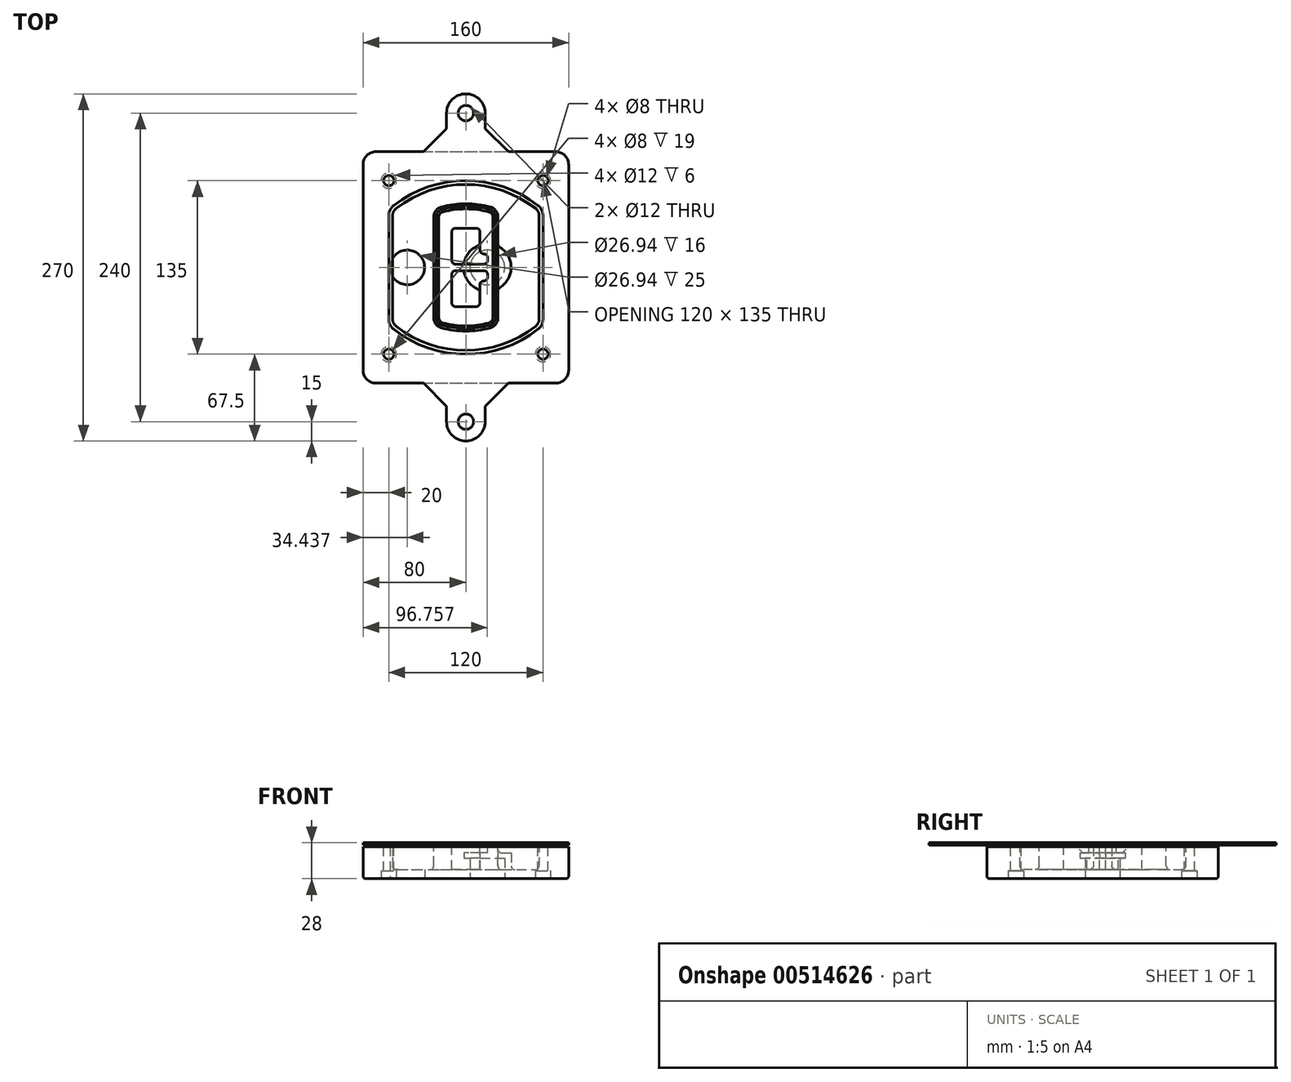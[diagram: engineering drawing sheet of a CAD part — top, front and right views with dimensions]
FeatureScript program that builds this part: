
annotation { "Feature Type Name" : "Feature", "Feature Type Description" : "" }
export const myFeature = defineFeature(function(context is Context, id is Id, definition is map)
    precondition{}
    {
        {
            var Q0;
            Q0=qCreatedBy(makeId("Top.planeOp"),FACE);
            var sketch = newSketch(context, id + "F0", { "sketchPlane" : qUnion([Q0])});
            skPoint(sketch, "E0.rect.middle", {"position": v(0, 0) * mm});
            skLineSegment(sketch, "E1.bottom", {"start": v(-70, -90) * mm, "end": v(70, -90) * mm});
            skLineSegment(sketch, "E1.top", {"start": v(-70, 90) * mm, "end": v(70, 90) * mm});
            skLineSegment(sketch, "E1.left", {"start": v(-80, -80) * mm, "end": v(-80, 80) * mm});
            skLineSegment(sketch, "E1.right", {"start": v(80, -80) * mm, "end": v(80, 80) * mm});
            skLineSegment(sketch, "E2", {"start": v(-80, 90) * mm, "end": v(80, -90) * mm, "construction": true});
            skLineSegment(sketch, "E3", {"start": v(80, 90) * mm, "end": v(-80, -90) * mm, "construction": true});
            skCircle(sketch, "E4", {"center": v(-60, 67.5) * mm, "radius": 4 * mm});
            skCircle(sketch, "E5", {"center": v(60, 67.5) * mm, "radius": 4 * mm});
            skCircle(sketch, "E6", {"center": v(60, -67.5) * mm, "radius": 4 * mm});
            skCircle(sketch, "E7", {"center": v(-60, -67.5) * mm, "radius": 4 * mm});
            skLineSegment(sketch, "E8", {"start": v(-60, 67.5) * mm, "end": v(60, 67.5) * mm, "construction": true});
            skLineSegment(sketch, "E9", {"start": v(60, 67.5) * mm, "end": v(60, -67.5) * mm, "construction": true});
            skLineSegment(sketch, "E10", {"start": v(60, -67.5) * mm, "end": v(-60, -67.5) * mm, "construction": true});
            skLineSegment(sketch, "E11", {"start": v(-60, -67.5) * mm, "end": v(-60, 67.5) * mm, "construction": true});
            skLineSegment(sketch, "E12", {"start": v(-60, 40.3) * mm, "end": v(-60, -40.3) * mm});
            skLineSegment(sketch, "E13", {"start": v(60, 40.3) * mm, "end": v(60, -40.3) * mm});
            skArc(sketch, "E14", {"start": v(56.15, 48.18) * mm, "mid": v(0, 67.5) * mm, "end": v(-56.15, 48.18) * mm});
            skArc(sketch, "E15", {"start": v(-56.15, -48.18) * mm, "mid": v(0, -67.5) * mm, "end": v(56.15, -48.18) * mm});
            skLineSegment(sketch, "E16", {"start": v(-60, 0) * mm, "end": v(60, 0) * mm, "construction": true});
            skPoint(sketch, "E17.visualSharp", {"position": v(-60, -45) * mm});
            skArc(sketch, "E17.filletArc", {"start": v(-60, -40.3) * mm, "mid": v(-58.99, -44.68) * mm, "end": v(-56.15, -48.18) * mm});
            skPoint(sketch, "E18.visualSharp", {"position": v(-60, 45) * mm});
            skArc(sketch, "E18.filletArc", {"start": v(-56.15, 48.18) * mm, "mid": v(-58.99, 44.68) * mm, "end": v(-60, 40.3) * mm});
            skPoint(sketch, "E19.visualSharp", {"position": v(60, 45) * mm});
            skArc(sketch, "E19.filletArc", {"start": v(60, 40.3) * mm, "mid": v(58.99, 44.68) * mm, "end": v(56.15, 48.18) * mm});
            skPoint(sketch, "E20.visualSharp", {"position": v(60, -45) * mm});
            skArc(sketch, "E20.filletArc", {"start": v(56.15, -48.18) * mm, "mid": v(58.99, -44.68) * mm, "end": v(60, -40.3) * mm});
            skPoint(sketch, "E21.visualSharp", {"position": v(-80, 90) * mm});
            skArc(sketch, "E21.filletArc", {"start": v(-70, 90) * mm, "mid": v(-77.07, 87.07) * mm, "end": v(-80, 80) * mm});
            skPoint(sketch, "E22.visualSharp", {"position": v(80, 90) * mm});
            skArc(sketch, "E22.filletArc", {"start": v(80, 80) * mm, "mid": v(77.07, 87.07) * mm, "end": v(70, 90) * mm});
            skPoint(sketch, "E23.visualSharp", {"position": v(80, -90) * mm});
            skArc(sketch, "E23.filletArc", {"start": v(70, -90) * mm, "mid": v(77.07, -87.07) * mm, "end": v(80, -80) * mm});
            skPoint(sketch, "E24.visualSharp", {"position": v(-80, -90) * mm});
            skArc(sketch, "E24.filletArc", {"start": v(-80, -80) * mm, "mid": v(-77.07, -87.07) * mm, "end": v(-70, -90) * mm});
            skArc(sketch, "E25.0", {"start": v(57, 40.3) * mm, "mid": v(56.3, 43.36) * mm, "end": v(54.3, 45.81) * mm});
            skLineSegment(sketch, "E25.1", {"start": v(57, 40.3) * mm, "end": v(57, -40.3) * mm});
            skArc(sketch, "E25.2", {"start": v(54.3, -45.81) * mm, "mid": v(56.3, -43.36) * mm, "end": v(57, -40.3) * mm});
            skArc(sketch, "E25.3", {"start": v(-54.3, -45.81) * mm, "mid": v(0, -64.5) * mm, "end": v(54.3, -45.81) * mm});
            skArc(sketch, "E25.4", {"start": v(-57, -40.3) * mm, "mid": v(-56.3, -43.36) * mm, "end": v(-54.3, -45.81) * mm});
            skArc(sketch, "E25.5", {"start": v(54.3, 45.81) * mm, "mid": v(0, 64.5) * mm, "end": v(-54.3, 45.81) * mm});
            skLineSegment(sketch, "E25.6", {"start": v(-57, 40.3) * mm, "end": v(-57, -40.3) * mm});
            skArc(sketch, "E25.7", {"start": v(-54.3, 45.81) * mm, "mid": v(-56.3, 43.36) * mm, "end": v(-57, 40.3) * mm});
            skArc(sketch, "E26.0", {"start": v(-58.62, 51.33) * mm, "mid": v(-62.58, 46.43) * mm, "end": v(-64, 40.3) * mm});
            skArc(sketch, "E26.1", {"start": v(58.62, 51.33) * mm, "mid": v(0, 71.5) * mm, "end": v(-58.62, 51.33) * mm});
            skArc(sketch, "E26.2", {"start": v(64, 40.3) * mm, "mid": v(62.58, 46.43) * mm, "end": v(58.62, 51.33) * mm});
            skLineSegment(sketch, "E26.3", {"start": v(64, 40.3) * mm, "end": v(64, -40.3) * mm});
            skArc(sketch, "E26.4", {"start": v(58.62, -51.33) * mm, "mid": v(62.58, -46.43) * mm, "end": v(64, -40.3) * mm});
            skLineSegment(sketch, "E26.5", {"start": v(-64, 40.3) * mm, "end": v(-64, -40.3) * mm});
            skArc(sketch, "E26.6", {"start": v(-58.62, -51.33) * mm, "mid": v(0, -71.5) * mm, "end": v(58.62, -51.33) * mm});
            skArc(sketch, "E26.7", {"start": v(-64, -40.3) * mm, "mid": v(-62.58, -46.43) * mm, "end": v(-58.62, -51.33) * mm});
            skSolve(sketch);
        }
        {
            var Q0;
            Q0=makeQuery(id+"F0.imprint","IMPRINT",FACE,{"disambiguationData":[TD([[makeQuery(id+"F0.imprint","IMPRINT",EDGE,{"derivedFrom":sQuery(id+"F0.wireOp",EDGE,"E1.bottom")}),1.0]])]});
            var Q1;
            Q1=makeQuery(id+"F0.imprint","IMPRINT",FACE,{"disambiguationData":[TD([[makeQuery(id+"F0.imprint","IMPRINT",EDGE,{"derivedFrom":sQuery(id+"F0.wireOp",EDGE,"E12")}),1.0]])]});
            var Q2;
            Q2=makeQuery(id+"F0.imprint","IMPRINT",FACE,{"disambiguationData":[TD([[makeQuery(id+"F0.imprint","IMPRINT",EDGE,{"derivedFrom":sQuery(id+"F0.wireOp",EDGE,"E25.0")}),1.0]])]});
            var Q3;
            Q3=makeQuery(id+"F0.imprint","IMPRINT",FACE,{"disambiguationData":[TD([[makeQuery(id+"F0.imprint","IMPRINT",EDGE,{"derivedFrom":sQuery(id+"F0.wireOp",EDGE,"E12")}),-1.0]])]});
            extrude(context, id + "F1", {"entities" : qUnion([Q0, Q1, Q2, Q3]), "oppositeDirection" : true, "depth" : 25 * mm});
        }
        {
            var Q0;
            Q0=makeQuery(id+"F0.imprint","IMPRINT",FACE,{"disambiguationData":[TD([[makeQuery(id+"F0.imprint","IMPRINT",EDGE,{"derivedFrom":sQuery(id+"F0.wireOp",EDGE,"E12")}),1.0]])]});
            extrude(context, id + "F2", {"entities" : qUnion([Q0]), "operationType" : NewBodyOperationType.ADD, "depth" : 3 * mm});
        }
        {
            var Q0;
            Q0=makeQuery(id+"F0.imprint","IMPRINT",FACE,{"disambiguationData":[TD([[makeQuery(id+"F0.imprint","IMPRINT",EDGE,{"derivedFrom":sQuery(id+"F0.wireOp",EDGE,"E25.0")}),1.0]])]});
            extrude(context, id + "F3", {"entities" : qUnion([Q0]), "operationType" : NewBodyOperationType.REMOVE, "oppositeDirection" : true, "depth" : 18 * mm});
        }
        {
            var Q0;
            Q0=makeQuery(id+"F2.opExtrude","CAP_FACE",FACE,{"disambiguationData":[OSD([sQuery(id+"F0.wireOp",EDGE,"E12"),sQuery(id+"F0.wireOp",EDGE,"E13"),sQuery(id+"F0.wireOp",EDGE,"E14"),sQuery(id+"F0.wireOp",EDGE,"E15"),sQuery(id+"F0.wireOp",EDGE,"E17.filletArc"),sQuery(id+"F0.wireOp",EDGE,"E18.filletArc"),sQuery(id+"F0.wireOp",EDGE,"E19.filletArc"),sQuery(id+"F0.wireOp",EDGE,"E20.filletArc"),sQuery(id+"F0.wireOp",EDGE,"E25.0"),sQuery(id+"F0.wireOp",EDGE,"E25.1"),sQuery(id+"F0.wireOp",EDGE,"E25.2"),sQuery(id+"F0.wireOp",EDGE,"E25.3"),sQuery(id+"F0.wireOp",EDGE,"E25.4"),sQuery(id+"F0.wireOp",EDGE,"E25.5"),sQuery(id+"F0.wireOp",EDGE,"E25.6"),sQuery(id+"F0.wireOp",EDGE,"E25.7")])],"isStart":false});
            var sketch = newSketch(context, id + "F4", { "sketchPlane" : qUnion([Q0])});
            skArc(sketch, "E27.0", {"start": v(-19.08, -46.97) * mm, "mid": v(0, -49.5) * mm, "end": v(19.08, -46.97) * mm});
            skArc(sketch, "E28.0", {"start": v(19.08, 46.97) * mm, "mid": v(0, 49.5) * mm, "end": v(-19.08, 46.97) * mm});
            skLineSegment(sketch, "E29", {"start": v(-25, 39.25) * mm, "end": v(-25, -39.25) * mm});
            skLineSegment(sketch, "E30", {"start": v(25, 39.25) * mm, "end": v(25, -39.25) * mm});
            skLineSegment(sketch, "E31", {"start": v(-25, 45.1) * mm, "end": v(25, 45.1) * mm, "construction": true});
            skLineSegment(sketch, "E32", {"start": v(-25, -45.1) * mm, "end": v(25, -45.1) * mm, "construction": true});
            skPoint(sketch, "E33.visualSharp", {"position": v(-25, 45.1) * mm});
            skArc(sketch, "E33.filletArc", {"start": v(-19.08, 46.97) * mm, "mid": v(-23.35, 44.11) * mm, "end": v(-25, 39.25) * mm});
            skPoint(sketch, "E34.visualSharp", {"position": v(25, 45.1) * mm});
            skArc(sketch, "E34.filletArc", {"start": v(25, 39.25) * mm, "mid": v(23.35, 44.11) * mm, "end": v(19.08, 46.97) * mm});
            skPoint(sketch, "E35.visualSharp", {"position": v(25, -45.1) * mm});
            skArc(sketch, "E35.filletArc", {"start": v(19.08, -46.97) * mm, "mid": v(23.35, -44.11) * mm, "end": v(25, -39.25) * mm});
            skPoint(sketch, "E36.visualSharp", {"position": v(-25, -45.1) * mm});
            skArc(sketch, "E36.filletArc", {"start": v(-25, -39.25) * mm, "mid": v(-23.35, -44.11) * mm, "end": v(-19.08, -46.97) * mm});
            skArc(sketch, "E37.0", {"start": v(54.3, 45.81) * mm, "mid": v(0, 64.5) * mm, "end": v(-54.3, 45.81) * mm});
            skArc(sketch, "E37.1", {"start": v(-54.3, 45.81) * mm, "mid": v(-56.3, 43.36) * mm, "end": v(-57, 40.3) * mm});
            skLineSegment(sketch, "E37.2", {"start": v(-57, 40.3) * mm, "end": v(-57, -40.3) * mm});
            skArc(sketch, "E37.3", {"start": v(-57, -40.3) * mm, "mid": v(-56.3, -43.36) * mm, "end": v(-54.3, -45.81) * mm});
            skArc(sketch, "E37.4", {"start": v(-54.3, -45.81) * mm, "mid": v(0, -64.5) * mm, "end": v(54.3, -45.81) * mm});
            skArc(sketch, "E37.5", {"start": v(54.3, -45.81) * mm, "mid": v(56.3, -43.36) * mm, "end": v(57, -40.3) * mm});
            skLineSegment(sketch, "E37.6", {"start": v(57, 40.3) * mm, "end": v(57, -40.3) * mm});
            skArc(sketch, "E37.7", {"start": v(57, 40.3) * mm, "mid": v(56.3, 43.36) * mm, "end": v(54.3, 45.81) * mm});
            skLineSegment(sketch, "E38.0", {"start": v(23, 39.25) * mm, "end": v(23, -39.25) * mm});
            skArc(sketch, "E38.1", {"start": v(18.56, -45.04) * mm, "mid": v(21.76, -42.9) * mm, "end": v(23, -39.25) * mm});
            skArc(sketch, "E38.2", {"start": v(-18.56, -45.04) * mm, "mid": v(0, -47.5) * mm, "end": v(18.56, -45.04) * mm});
            skArc(sketch, "E38.3", {"start": v(-23, -39.25) * mm, "mid": v(-21.76, -42.9) * mm, "end": v(-18.56, -45.04) * mm});
            skLineSegment(sketch, "E38.4", {"start": v(-23, 39.25) * mm, "end": v(-23, -39.25) * mm});
            skArc(sketch, "E38.5", {"start": v(23, 39.25) * mm, "mid": v(21.76, 42.9) * mm, "end": v(18.56, 45.04) * mm});
            skArc(sketch, "E38.6", {"start": v(-18.56, 45.04) * mm, "mid": v(-21.76, 42.9) * mm, "end": v(-23, 39.25) * mm});
            skArc(sketch, "E38.7", {"start": v(18.56, 45.04) * mm, "mid": v(0, 47.5) * mm, "end": v(-18.56, 45.04) * mm});
            skArc(sketch, "E39.0", {"start": v(21, 39.25) * mm, "mid": v(20.18, 41.68) * mm, "end": v(18.04, 43.1) * mm});
            skLineSegment(sketch, "E39.1", {"start": v(21, 39.25) * mm, "end": v(21, -39.25) * mm});
            skArc(sketch, "E39.2", {"start": v(18.04, -43.1) * mm, "mid": v(20.18, -41.68) * mm, "end": v(21, -39.25) * mm});
            skArc(sketch, "E39.3", {"start": v(-18.04, -43.1) * mm, "mid": v(0, -45.5) * mm, "end": v(18.04, -43.1) * mm});
            skArc(sketch, "E39.4", {"start": v(-21, -39.25) * mm, "mid": v(-20.18, -41.68) * mm, "end": v(-18.04, -43.1) * mm});
            skArc(sketch, "E39.5", {"start": v(18.04, 43.1) * mm, "mid": v(0, 45.5) * mm, "end": v(-18.04, 43.1) * mm});
            skLineSegment(sketch, "E39.6", {"start": v(-21, 39.25) * mm, "end": v(-21, -39.25) * mm});
            skArc(sketch, "E39.7", {"start": v(-18.04, 43.1) * mm, "mid": v(-20.18, 41.68) * mm, "end": v(-21, 39.25) * mm});
            skLineSegment(sketch, "E40", {"start": v(-25, 0) * mm, "end": v(25, 0) * mm, "construction": true});
            skLineSegment(sketch, "E41", {"start": v(-11, 5.5) * mm, "end": v(-11, 27.5) * mm});
            skLineSegment(sketch, "E42", {"start": v(-8, 30.5) * mm, "end": v(8, 30.5) * mm});
            skLineSegment(sketch, "E43", {"start": v(11, 27.5) * mm, "end": v(11, 13.5) * mm});
            skLineSegment(sketch, "E44", {"start": v(14, 10.5) * mm, "end": v(14, 10.5) * mm});
            skLineSegment(sketch, "E45", {"start": v(17, 7.5) * mm, "end": v(17, 5.5) * mm});
            skLineSegment(sketch, "E46", {"start": v(14, 2.5) * mm, "end": v(-8, 2.5) * mm});
            skPoint(sketch, "E47.visualSharp", {"position": v(-11, 30.5) * mm});
            skArc(sketch, "E47.filletArc", {"start": v(-8, 30.5) * mm, "mid": v(-10.12, 29.62) * mm, "end": v(-11, 27.5) * mm});
            skPoint(sketch, "E48.visualSharp", {"position": v(11, 30.5) * mm});
            skArc(sketch, "E48.filletArc", {"start": v(11, 27.5) * mm, "mid": v(10.12, 29.62) * mm, "end": v(8, 30.5) * mm});
            skPoint(sketch, "E49.visualSharp", {"position": v(11, 10.5) * mm});
            skArc(sketch, "E49.filletArc", {"start": v(11, 13.5) * mm, "mid": v(11.88, 11.38) * mm, "end": v(14, 10.5) * mm});
            skPoint(sketch, "E50.visualSharp", {"position": v(17, 10.5) * mm});
            skArc(sketch, "E50.filletArc", {"start": v(17, 7.5) * mm, "mid": v(16.12, 9.62) * mm, "end": v(14, 10.5) * mm});
            skPoint(sketch, "E51.visualSharp", {"position": v(17, 2.5) * mm});
            skArc(sketch, "E51.filletArc", {"start": v(14, 2.5) * mm, "mid": v(16.12, 3.38) * mm, "end": v(17, 5.5) * mm});
            skPoint(sketch, "E52.visualSharp", {"position": v(-11, 2.5) * mm});
            skArc(sketch, "E52.filletArc", {"start": v(-11, 5.5) * mm, "mid": v(-10.12, 3.38) * mm, "end": v(-8, 2.5) * mm});
            skLineSegment(sketch, "E53.0.MirrorCS", {"start": v(14, -2.5) * mm, "end": v(-8, -2.5) * mm});
            skArc(sketch, "E54.0.MirrorCS", {"start": v(-11, -5.5) * mm, "mid": v(-10.12, -3.38) * mm, "end": v(-8, -2.5) * mm});
            skLineSegment(sketch, "E55.0.MirrorCS", {"start": v(-11, -5.5) * mm, "end": v(-11, -27.5) * mm});
            skArc(sketch, "E56.0.MirrorCS", {"start": v(-8, -30.5) * mm, "mid": v(-10.12, -29.62) * mm, "end": v(-11, -27.5) * mm});
            skLineSegment(sketch, "E57.0.MirrorCS", {"start": v(-8, -30.5) * mm, "end": v(8, -30.5) * mm});
            skArc(sketch, "E58.0.MirrorCS", {"start": v(11, -27.5) * mm, "mid": v(10.12, -29.62) * mm, "end": v(8, -30.5) * mm});
            skLineSegment(sketch, "E59.0.MirrorCS", {"start": v(11, -27.5) * mm, "end": v(11, -13.5) * mm});
            skArc(sketch, "E60.0.MirrorCS", {"start": v(11, -13.5) * mm, "mid": v(11.88, -11.38) * mm, "end": v(14, -10.5) * mm});
            skArc(sketch, "E61.0.MirrorCS", {"start": v(17, -7.5) * mm, "mid": v(16.12, -9.62) * mm, "end": v(14, -10.5) * mm});
            skLineSegment(sketch, "E62.0.MirrorCS", {"start": v(17, -7.5) * mm, "end": v(17, -5.5) * mm});
            skArc(sketch, "E63.0.MirrorCS", {"start": v(14, -2.5) * mm, "mid": v(16.12, -3.38) * mm, "end": v(17, -5.5) * mm});
            skSolve(sketch);
        }
        {
            var Q0;
            Q0=makeQuery(id+"F4.imprint","IMPRINT",FACE,{"disambiguationData":[TD([[makeQuery(id+"F4.imprint","IMPRINT",EDGE,{"derivedFrom":sQuery(id+"F4.wireOp",EDGE,"E27.0")}),1.0]])]});
            var Q1;
            Q1=makeQuery(id+"F4.imprint","IMPRINT",FACE,{"disambiguationData":[TD([[makeQuery(id+"F4.imprint","IMPRINT",EDGE,{"derivedFrom":sQuery(id+"F4.wireOp",EDGE,"E38.0")}),-1.0]])]});
            var Q2;
            Q2=makeQuery(id+"F4.imprint","IMPRINT",FACE,{"disambiguationData":[TD([[makeQuery(id+"F4.imprint","IMPRINT",EDGE,{"derivedFrom":sQuery(id+"F4.wireOp",EDGE,"E39.0")}),1.0]])]});
            extrude(context, id + "F5", {"entities" : qUnion([Q0, Q1, Q2]), "operationType" : NewBodyOperationType.ADD, "endBound" : BoundingType.UP_TO_NEXT, "oppositeDirection" : true, "depth" : 25 * mm});
        }
        {
            var Q0;
            Q0=makeQuery(id+"F4.imprint","IMPRINT",FACE,{"disambiguationData":[TD([[makeQuery(id+"F4.imprint","IMPRINT",EDGE,{"derivedFrom":sQuery(id+"F4.wireOp",EDGE,"E38.0")}),-1.0]])]});
            extrude(context, id + "F6", {"entities" : qUnion([Q0]), "operationType" : NewBodyOperationType.REMOVE, "oppositeDirection" : true, "depth" : 2 * mm});
        }
        {
            var Q0;
            Q0=makeQuery(id+"F1.opExtrude","CAP_FACE",FACE,{"disambiguationData":[OSD([sQuery(id+"F0.wireOp",EDGE,"E1.bottom"),sQuery(id+"F0.wireOp",EDGE,"E1.top"),sQuery(id+"F0.wireOp",EDGE,"E1.left"),sQuery(id+"F0.wireOp",EDGE,"E1.right"),sQuery(id+"F0.wireOp",EDGE,"E4"),sQuery(id+"F0.wireOp",EDGE,"E5"),sQuery(id+"F0.wireOp",EDGE,"E6"),sQuery(id+"F0.wireOp",EDGE,"E7"),sQuery(id+"F0.wireOp",EDGE,"E21.filletArc"),sQuery(id+"F0.wireOp",EDGE,"E22.filletArc"),sQuery(id+"F0.wireOp",EDGE,"E23.filletArc"),sQuery(id+"F0.wireOp",EDGE,"E24.filletArc")])],"isStart":false});
            var sketch = newSketch(context, id + "F7", { "sketchPlane" : qUnion([Q0])});
            skCircle(sketch, "E64", {"center": v(16.76, 0) * mm, "radius": 13.47 * mm});
            skCircle(sketch, "E65", {"center": v(-45.56, 0) * mm, "radius": 13.47 * mm});
            skLineSegment(sketch, "E66", {"start": v(80, 0) * mm, "end": v(-80, 0) * mm});
            skCircle(sketch, "E67", {"center": v(16.76, 0) * mm, "radius": 18.47 * mm});
            skCircle(sketch, "E68", {"center": v(60, -67.5) * mm, "radius": 6 * mm});
            skCircle(sketch, "E69", {"center": v(-60, -67.5) * mm, "radius": 6 * mm});
            skCircle(sketch, "E70", {"center": v(-60, 67.5) * mm, "radius": 6 * mm});
            skCircle(sketch, "E71", {"center": v(60, 67.5) * mm, "radius": 6 * mm});
            skSolve(sketch);
        }
        {
            var Q0;
            {var subQ1=sQuery(id+"F7.wireOp",EDGE,"E66");var subQ4=sQuery(id+"F7.wireOp",EDGE,"E64");var subQ6=makeQuery(id+"F7.imprint","INTERSECT",VERTEX,{"disambiguationData":[OD(0.0)],"derivedFrom":[subQ4,subQ1]});Q0=makeQuery(id+"F7.imprint","IMPRINT",FACE,{"disambiguationData":[TD([[makeQuery(id+"F7.imprint","IMPRINT",EDGE,{"disambiguationData":[TD([[subQ6,-1.0]])],"derivedFrom":subQ4}),-1.0]])]});}
            var Q1;
            {var subQ0=sQuery(id+"F7.wireOp",EDGE,"E66");var subQ1=sQuery(id+"F7.wireOp",EDGE,"E64");var subQ3=makeQuery(id+"F7.imprint","INTERSECT",VERTEX,{"disambiguationData":[OD(0.0)],"derivedFrom":[subQ1,subQ0]});Q1=makeQuery(id+"F7.imprint","IMPRINT",FACE,{"disambiguationData":[TD([[makeQuery(id+"F7.imprint","IMPRINT",EDGE,{"disambiguationData":[TD([[subQ3,-1.0]])],"derivedFrom":subQ1}),1.0]])]});}
            var Q2;
            {var subQ0=sQuery(id+"F7.wireOp",EDGE,"E66");var subQ1=sQuery(id+"F7.wireOp",EDGE,"E64");var subQ3=makeQuery(id+"F7.imprint","INTERSECT",VERTEX,{"disambiguationData":[OD(0.0)],"derivedFrom":[subQ1,subQ0]});Q2=makeQuery(id+"F7.imprint","IMPRINT",FACE,{"disambiguationData":[TD([[makeQuery(id+"F7.imprint","IMPRINT",EDGE,{"disambiguationData":[TD([[subQ3,1.0]])],"derivedFrom":subQ1}),1.0]])]});}
            var Q3;
            {var subQ1=sQuery(id+"F7.wireOp",EDGE,"E66");var subQ4=sQuery(id+"F7.wireOp",EDGE,"E64");var subQ6=makeQuery(id+"F7.imprint","INTERSECT",VERTEX,{"disambiguationData":[OD(0.0)],"derivedFrom":[subQ4,subQ1]});Q3=makeQuery(id+"F7.imprint","IMPRINT",FACE,{"disambiguationData":[TD([[makeQuery(id+"F7.imprint","IMPRINT",EDGE,{"disambiguationData":[TD([[subQ6,1.0]])],"derivedFrom":subQ4}),-1.0]])]});}
            extrude(context, id + "F8", {"entities" : qUnion([Q0, Q1, Q2, Q3]), "operationType" : NewBodyOperationType.ADD, "oppositeDirection" : true, "depth" : 20 * mm});
        }
        {
            var Q0;
            {var subQ0=sQuery(id+"F7.wireOp",EDGE,"E66");var subQ1=sQuery(id+"F7.wireOp",EDGE,"E64");var subQ3=makeQuery(id+"F7.imprint","INTERSECT",VERTEX,{"disambiguationData":[OD(0.0)],"derivedFrom":[subQ1,subQ0]});Q0=makeQuery(id+"F7.imprint","IMPRINT",FACE,{"disambiguationData":[TD([[makeQuery(id+"F7.imprint","IMPRINT",EDGE,{"disambiguationData":[TD([[subQ3,-1.0]])],"derivedFrom":subQ1}),1.0]])]});}
            var Q1;
            {var subQ0=sQuery(id+"F7.wireOp",EDGE,"E66");var subQ1=sQuery(id+"F7.wireOp",EDGE,"E64");var subQ3=makeQuery(id+"F7.imprint","INTERSECT",VERTEX,{"disambiguationData":[OD(0.0)],"derivedFrom":[subQ1,subQ0]});Q1=makeQuery(id+"F7.imprint","IMPRINT",FACE,{"disambiguationData":[TD([[makeQuery(id+"F7.imprint","IMPRINT",EDGE,{"disambiguationData":[TD([[subQ3,1.0]])],"derivedFrom":subQ1}),1.0]])]});}
            extrude(context, id + "F9", {"entities" : qUnion([Q0, Q1]), "operationType" : NewBodyOperationType.REMOVE, "oppositeDirection" : true, "depth" : 16 * mm});
        }
        {
            var Q0;
            {var subQ0=sQuery(id+"F7.wireOp",EDGE,"E66");var subQ1=sQuery(id+"F7.wireOp",EDGE,"E65");var subQ3=makeQuery(id+"F7.imprint","INTERSECT",VERTEX,{"disambiguationData":[OD(0.0)],"derivedFrom":[subQ1,subQ0]});Q0=makeQuery(id+"F7.imprint","IMPRINT",FACE,{"disambiguationData":[TD([[makeQuery(id+"F7.imprint","IMPRINT",EDGE,{"disambiguationData":[TD([[subQ3,-1.0]])],"derivedFrom":subQ1}),1.0]])]});}
            var Q1;
            {var subQ0=sQuery(id+"F7.wireOp",EDGE,"E66");var subQ1=sQuery(id+"F7.wireOp",EDGE,"E65");var subQ3=makeQuery(id+"F7.imprint","INTERSECT",VERTEX,{"disambiguationData":[OD(0.0)],"derivedFrom":[subQ1,subQ0]});Q1=makeQuery(id+"F7.imprint","IMPRINT",FACE,{"disambiguationData":[TD([[makeQuery(id+"F7.imprint","IMPRINT",EDGE,{"disambiguationData":[TD([[subQ3,1.0]])],"derivedFrom":subQ1}),1.0]])]});}
            extrude(context, id + "F10", {"entities" : qUnion([Q0, Q1]), "operationType" : NewBodyOperationType.REMOVE, "oppositeDirection" : true, "depth" : 25 * mm});
        }
        {
            var Q0;
            Q0=makeQuery(id+"F7.imprint","IMPRINT",FACE,{"disambiguationData":[TD([[makeQuery(id+"F7.imprint","IMPRINT",EDGE,{"derivedFrom":sQuery(id+"F7.wireOp",EDGE,"E68")}),1.0]])]});
            var Q1;
            Q1=makeQuery(id+"F7.imprint","IMPRINT",FACE,{"disambiguationData":[TD([[makeQuery(id+"F7.imprint","IMPRINT",EDGE,{"derivedFrom":makeQuery(id+"F1.opExtrude","CAP_EDGE",EDGE,{"disambiguationData":[OSD([sQuery(id+"F0.wireOp",EDGE,"E5")])],"isStart":false})}),-1.0]])]});
            var Q2;
            Q2=makeQuery(id+"F7.imprint","IMPRINT",FACE,{"disambiguationData":[TD([[makeQuery(id+"F7.imprint","IMPRINT",EDGE,{"derivedFrom":sQuery(id+"F7.wireOp",EDGE,"E69")}),1.0]])]});
            var Q3;
            Q3=makeQuery(id+"F7.imprint","IMPRINT",FACE,{"disambiguationData":[TD([[makeQuery(id+"F7.imprint","IMPRINT",EDGE,{"derivedFrom":makeQuery(id+"F1.opExtrude","CAP_EDGE",EDGE,{"disambiguationData":[OSD([sQuery(id+"F0.wireOp",EDGE,"E4")])],"isStart":false})}),-1.0]])]});
            var Q4;
            Q4=makeQuery(id+"F7.imprint","IMPRINT",FACE,{"disambiguationData":[TD([[makeQuery(id+"F7.imprint","IMPRINT",EDGE,{"derivedFrom":sQuery(id+"F7.wireOp",EDGE,"E70")}),1.0]])]});
            var Q5;
            Q5=makeQuery(id+"F7.imprint","IMPRINT",FACE,{"disambiguationData":[TD([[makeQuery(id+"F7.imprint","IMPRINT",EDGE,{"derivedFrom":makeQuery(id+"F1.opExtrude","CAP_EDGE",EDGE,{"disambiguationData":[OSD([sQuery(id+"F0.wireOp",EDGE,"E7")])],"isStart":false})}),-1.0]])]});
            var Q6;
            Q6=makeQuery(id+"F7.imprint","IMPRINT",FACE,{"disambiguationData":[TD([[makeQuery(id+"F7.imprint","IMPRINT",EDGE,{"derivedFrom":sQuery(id+"F7.wireOp",EDGE,"E71")}),1.0]])]});
            var Q7;
            Q7=makeQuery(id+"F7.imprint","IMPRINT",FACE,{"disambiguationData":[TD([[makeQuery(id+"F7.imprint","IMPRINT",EDGE,{"derivedFrom":makeQuery(id+"F1.opExtrude","CAP_EDGE",EDGE,{"disambiguationData":[OSD([sQuery(id+"F0.wireOp",EDGE,"E6")])],"isStart":false})}),-1.0]])]});
            extrude(context, id + "F11", {"entities" : qUnion([Q0, Q1, Q2, Q3, Q4, Q5, Q6, Q7]), "operationType" : NewBodyOperationType.REMOVE, "oppositeDirection" : true, "depth" : 6 * mm});
        }
        {
            var Q0;
            Q0=makeQuery(id+"F9.boolean.opBoolean","COPY",FACE,{"derivedFrom":makeQuery(id+"F9.opExtrude","CAP_FACE",FACE,{"disambiguationData":[OSD([sQuery(id+"F7.wireOp",EDGE,"E64")])],"isStart":false})});
            var sketch = newSketch(context, id + "F12", { "sketchPlane" : qUnion([Q0])});
            skArc(sketch, "E72.0", {"start": v(11, 17.55) * mm, "mid": v(2.57, 11.82) * mm, "end": v(-1.54, 2.5) * mm});
            skArc(sketch, "E72.1", {"start": v(-1.54, -2.5) * mm, "mid": v(2.57, -11.82) * mm, "end": v(11, -17.55) * mm});
            skLineSegment(sketch, "E73", {"start": v(-1.54, -2.5) * mm, "end": v(14, -2.5) * mm});
            skLineSegment(sketch, "E74.0", {"start": v(14, 2.5) * mm, "end": v(-1.54, 2.5) * mm});
            skArc(sketch, "E74.1", {"start": v(14, 2.5) * mm, "mid": v(16.12, 3.38) * mm, "end": v(17, 5.5) * mm});
            skLineSegment(sketch, "E74.2", {"start": v(17, 7.5) * mm, "end": v(17, 5.5) * mm});
            skArc(sketch, "E74.3", {"start": v(17, 7.5) * mm, "mid": v(16.12, 9.62) * mm, "end": v(14, 10.5) * mm});
            skArc(sketch, "E74.4", {"start": v(11, 13.5) * mm, "mid": v(11.88, 11.38) * mm, "end": v(14, 10.5) * mm});
            skLineSegment(sketch, "E74.5", {"start": v(11, 17.55) * mm, "end": v(11, 13.5) * mm});
            skLineSegment(sketch, "E74.7", {"start": v(14, -2.5) * mm, "end": v(-1.54, -2.5) * mm});
            skArc(sketch, "E74.8", {"start": v(14, -2.5) * mm, "mid": v(16.12, -3.38) * mm, "end": v(17, -5.5) * mm});
            skLineSegment(sketch, "E74.9", {"start": v(17, -7.5) * mm, "end": v(17, -5.5) * mm});
            skArc(sketch, "E74.10", {"start": v(17, -7.5) * mm, "mid": v(16.12, -9.62) * mm, "end": v(14, -10.5) * mm});
            skArc(sketch, "E74.11", {"start": v(11, -13.5) * mm, "mid": v(11.88, -11.38) * mm, "end": v(14, -10.5) * mm});
            skLineSegment(sketch, "E74.12", {"start": v(11, -17.55) * mm, "end": v(11, -13.5) * mm});
            skPoint(sketch, "E75.orphan", {"position": v(11, -27.5) * mm});
            skPoint(sketch, "E76.orphan", {"position": v(-8, -2.5) * mm});
            skPoint(sketch, "E77.orphan", {"position": v(-8, 2.5) * mm});
            skPoint(sketch, "E78.orphan", {"position": v(11, 27.5) * mm});
            skSolve(sketch);
        }
        {
            var Q0;
            {var subQ7=sQuery(id+"F12.wireOp",EDGE,"E72.0");var subQ14=sQuery(id+"F12.wireOp",EDGE,"E72.1");var subQ16=sQuery(id+"F12.wireOp",EDGE,"E74.1");var subQ18=sQuery(id+"F12.wireOp",EDGE,"E74.8");Q0=qUnion([makeQuery(id+"F12.imprint","IMPRINT",FACE,{"disambiguationData":[TD([[makeQuery(id+"F12.imprint","IMPRINT",EDGE,{"derivedFrom":subQ7}),1.0]])]}),makeQuery(id+"F12.imprint","IMPRINT",FACE,{"disambiguationData":[TD([[makeQuery(id+"F12.imprint","IMPRINT",EDGE,{"derivedFrom":subQ14}),1.0]])]}),makeQuery(id+"F12.imprint","IMPRINT",FACE,{"disambiguationData":[TD([[makeQuery(id+"F12.imprint","IMPRINT",EDGE,{"derivedFrom":subQ16}),1.0]])]}),makeQuery(id+"F12.imprint","IMPRINT",FACE,{"disambiguationData":[TD([[makeQuery(id+"F12.imprint","IMPRINT",EDGE,{"derivedFrom":subQ18}),-1.0]])]})]);}
            var Q1;
            Q1=makeQuery(id+"F5.boolean.opBoolean","SPLIT",FACE,{"disambiguationData":[TD([makeQuery(id+"F5.opExtrude","SWEPT_FACE",FACE,{"disambiguationData":[OSD([sQuery(id+"F4.wireOp",EDGE,"E41")])]})])],"derivedFrom":makeQuery(id+"F3.boolean.opBoolean","COPY",FACE,{"derivedFrom":makeQuery(id+"F3.opExtrude","CAP_FACE",FACE,{"disambiguationData":[OSD([sQuery(id+"F0.wireOp",EDGE,"E25.0"),sQuery(id+"F0.wireOp",EDGE,"E25.1"),sQuery(id+"F0.wireOp",EDGE,"E25.2"),sQuery(id+"F0.wireOp",EDGE,"E25.3"),sQuery(id+"F0.wireOp",EDGE,"E25.4"),sQuery(id+"F0.wireOp",EDGE,"E25.5"),sQuery(id+"F0.wireOp",EDGE,"E25.6"),sQuery(id+"F0.wireOp",EDGE,"E25.7")])],"isStart":false})})});
            extrude(context, id + "F13", {"entities" : qUnion([Q0]), "operationType" : NewBodyOperationType.REMOVE, "endBound" : BoundingType.UP_TO_SURFACE, "endBoundEntityFace" : qUnion([Q1]), "depth" : 25 * mm});
        }
        {
            var Q0;
            Q0=makeQuery(id+"F3.boolean.opBoolean","COPY",EDGE,{"derivedFrom":makeQuery(id+"F3.opExtrude","CAP_EDGE",EDGE,{"disambiguationData":[OSD([sQuery(id+"F0.wireOp",EDGE,"E25.6")])],"isStart":false})});
            var Q1;
            Q1=makeQuery(id+"F8.boolean.opBoolean","INTERSECT",EDGE,{"derivedFrom":[makeQuery(id+"F5.opExtrude","SWEPT_FACE",FACE,{"disambiguationData":[OSD([sQuery(id+"F4.wireOp",EDGE,"E30")])]}),makeQuery(id+"F8.opExtrude","CAP_FACE",FACE,{"disambiguationData":[OSD([sQuery(id+"F7.wireOp",EDGE,"E67")])],"isStart":false})]});
            var Q2;
            Q2=makeQuery(id+"F8.boolean.opBoolean","INTERSECT",EDGE,{"disambiguationData":[OD(1.0)],"derivedFrom":[makeQuery(id+"F5.opExtrude","SWEPT_FACE",FACE,{"disambiguationData":[OSD([sQuery(id+"F4.wireOp",EDGE,"E30")])]}),makeQuery(id+"F8.opExtrude","SWEPT_FACE",FACE,{"disambiguationData":[OSD([sQuery(id+"F7.wireOp",EDGE,"E67")])]})]});
            var Q3;
            {var subQ0=sQuery(id+"F4.wireOp",EDGE,"E30");Q3=makeQuery(id+"F8.boolean.opBoolean","SPLIT",EDGE,{"disambiguationData":[TD([makeQuery(id+"F5.opExtrude","SWEPT_FACE",FACE,{"disambiguationData":[OSD([sQuery(id+"F4.wireOp",EDGE,"E35.filletArc")])]})])],"derivedFrom":makeQuery(id+"F5.opExtrude","CAP_EDGE",EDGE,{"disambiguationData":[OSD([subQ0])],"isStart":false})});}
            var Q4;
            {var subQ0=sQuery(id+"F0.wireOp",EDGE,"E25.7");var subQ1=sQuery(id+"F0.wireOp",EDGE,"E25.1");var subQ2=sQuery(id+"F0.wireOp",EDGE,"E25.6");var subQ3=sQuery(id+"F0.wireOp",EDGE,"E25.5");var subQ4=sQuery(id+"F0.wireOp",EDGE,"E25.4");var subQ5=sQuery(id+"F0.wireOp",EDGE,"E25.0");var subQ6=sQuery(id+"F0.wireOp",EDGE,"E25.2");var subQ7=sQuery(id+"F0.wireOp",EDGE,"E25.3");Q4=makeQuery(id+"F8.boolean.opBoolean","INTERSECT",EDGE,{"derivedFrom":[makeQuery(id+"F5.boolean.opBoolean","SPLIT",FACE,{"disambiguationData":[TD([makeQuery(id+"F2.opExtrude","SWEPT_FACE",FACE,{"disambiguationData":[OSD([subQ5])]})])],"derivedFrom":makeQuery(id+"F3.boolean.opBoolean","COPY",FACE,{"derivedFrom":makeQuery(id+"F3.opExtrude","CAP_FACE",FACE,{"disambiguationData":[OSD([subQ5,subQ1,subQ6,subQ7,subQ4,subQ3,subQ2,subQ0])],"isStart":false})})}),makeQuery(id+"F8.opExtrude","SWEPT_FACE",FACE,{"disambiguationData":[OSD([sQuery(id+"F7.wireOp",EDGE,"E67")])]})]});}
            var Q5;
            Q5=makeQuery(id+"F8.boolean.opBoolean","INTERSECT",EDGE,{"disambiguationData":[OD(0.0)],"derivedFrom":[makeQuery(id+"F5.opExtrude","SWEPT_FACE",FACE,{"disambiguationData":[OSD([sQuery(id+"F4.wireOp",EDGE,"E30")])]}),makeQuery(id+"F8.opExtrude","SWEPT_FACE",FACE,{"disambiguationData":[OSD([sQuery(id+"F7.wireOp",EDGE,"E67")])]})]});
            fillet(context, id + "F14", {"entities" : qUnion([Q0, Q1, Q2, Q3, Q4, Q5]), "radius" : 3 * mm, "tangentPropagation" : true, "allowEdgeOverflow" : false});
        }
        {
            var Q0;
            Q0=makeQuery(id+"F1.opExtrude","CAP_EDGE",EDGE,{"disambiguationData":[OSD([sQuery(id+"F0.wireOp",EDGE,"E1.bottom")])],"isStart":false});
            fillet(context, id + "F15", {"entities" : qUnion([Q0]), "radius" : 2 * mm, "tangentPropagation" : true, "allowEdgeOverflow" : false});
        }
        {
            var Q0;
            Q0=makeQuery(id+"F6.boolean.opBoolean","COPY",FACE,{"derivedFrom":makeQuery(id+"F6.opExtrude","CAP_FACE",FACE,{"disambiguationData":[OSD([sQuery(id+"F4.wireOp",EDGE,"E38.0"),sQuery(id+"F4.wireOp",EDGE,"E38.1"),sQuery(id+"F4.wireOp",EDGE,"E38.2"),sQuery(id+"F4.wireOp",EDGE,"E38.3"),sQuery(id+"F4.wireOp",EDGE,"E38.4"),sQuery(id+"F4.wireOp",EDGE,"E38.5"),sQuery(id+"F4.wireOp",EDGE,"E38.6"),sQuery(id+"F4.wireOp",EDGE,"E38.7"),sQuery(id+"F4.wireOp",EDGE,"E39.0"),sQuery(id+"F4.wireOp",EDGE,"E39.1"),sQuery(id+"F4.wireOp",EDGE,"E39.2"),sQuery(id+"F4.wireOp",EDGE,"E39.3"),sQuery(id+"F4.wireOp",EDGE,"E39.4"),sQuery(id+"F4.wireOp",EDGE,"E39.5"),sQuery(id+"F4.wireOp",EDGE,"E39.6"),sQuery(id+"F4.wireOp",EDGE,"E39.7")])],"isStart":false})});
            var sketch = newSketch(context, id + "F16", { "sketchPlane" : qUnion([Q0])});
            skLineSegment(sketch, "E79.0", {"start": v(-80, -80) * mm, "end": v(-80, 80) * mm});
            skLineSegment(sketch, "E79.1", {"start": v(-70, -90) * mm, "end": v(70, -90) * mm});
            skArc(sketch, "E79.2", {"start": v(-80, -80) * mm, "mid": v(-77.07, -87.07) * mm, "end": v(-70, -90) * mm});
            skLineSegment(sketch, "E79.3", {"start": v(-70, 90) * mm, "end": v(70, 90) * mm});
            skArc(sketch, "E79.4", {"start": v(-70, 90) * mm, "mid": v(-77.07, 87.07) * mm, "end": v(-80, 80) * mm});
            skArc(sketch, "E79.5", {"start": v(80, 80) * mm, "mid": v(77.07, 87.07) * mm, "end": v(70, 90) * mm});
            skLineSegment(sketch, "E79.6", {"start": v(80, -80) * mm, "end": v(80, 80) * mm});
            skArc(sketch, "E79.7", {"start": v(70, -90) * mm, "mid": v(77.07, -87.07) * mm, "end": v(80, -80) * mm});
            skCircle(sketch, "E79.8", {"center": v(60, -67.5) * mm, "radius": 4 * mm});
            skCircle(sketch, "E79.9", {"center": v(-60, -67.5) * mm, "radius": 4 * mm});
            skCircle(sketch, "E79.10", {"center": v(-60, 67.5) * mm, "radius": 4 * mm});
            skCircle(sketch, "E79.11", {"center": v(60, 67.5) * mm, "radius": 4 * mm});
            skLineSegment(sketch, "E79.12", {"start": v(-60, 40.3) * mm, "end": v(-60, -40.3) * mm});
            skArc(sketch, "E79.13", {"start": v(-56.15, 48.18) * mm, "mid": v(-58.99, 44.68) * mm, "end": v(-60, 40.3) * mm});
            skArc(sketch, "E79.14", {"start": v(56.15, 48.18) * mm, "mid": v(0, 67.5) * mm, "end": v(-56.15, 48.18) * mm});
            skArc(sketch, "E79.15", {"start": v(60, 40.3) * mm, "mid": v(58.99, 44.68) * mm, "end": v(56.15, 48.18) * mm});
            skLineSegment(sketch, "E79.16", {"start": v(60, 40.3) * mm, "end": v(60, -40.3) * mm});
            skArc(sketch, "E79.17", {"start": v(-60, -40.3) * mm, "mid": v(-58.99, -44.68) * mm, "end": v(-56.15, -48.18) * mm});
            skArc(sketch, "E79.18", {"start": v(-56.15, -48.18) * mm, "mid": v(0, -67.5) * mm, "end": v(56.15, -48.18) * mm});
            skArc(sketch, "E79.19", {"start": v(56.15, -48.18) * mm, "mid": v(58.99, -44.68) * mm, "end": v(60, -40.3) * mm});
            skCircle(sketch, "E80", {"center": v(0, 120) * mm, "radius": 6 * mm});
            skLineSegment(sketch, "E81", {"start": v(-15, 120) * mm, "end": v(-15, 108) * mm});
            skLineSegment(sketch, "E82", {"start": v(-15, 108) * mm, "end": v(-33, 90) * mm});
            skLineSegment(sketch, "E83", {"start": v(0, 120) * mm, "end": v(0, 90) * mm, "construction": true});
            skArc(sketch, "E84", {"start": v(-15, 120) * mm, "mid": v(0, 135) * mm, "end": v(15, 120) * mm});
            skLineSegment(sketch, "E85", {"start": v(15, 120) * mm, "end": v(15, 108) * mm});
            skLineSegment(sketch, "E86", {"start": v(15, 108) * mm, "end": v(33, 90) * mm});
            skLineSegment(sketch, "E87", {"start": v(-80, 0) * mm, "end": v(80, 0) * mm, "construction": true});
            skArc(sketch, "E88.MirrorCS", {"start": v(-15, -120) * mm, "mid": v(0, -135) * mm, "end": v(15, -120) * mm});
            skLineSegment(sketch, "E89.MirrorCS", {"start": v(-15, -120) * mm, "end": v(-15, -108) * mm});
            skLineSegment(sketch, "E90.MirrorCS", {"start": v(-15, -108) * mm, "end": v(-33, -90) * mm});
            skLineSegment(sketch, "E91.MirrorCS", {"start": v(15, -108) * mm, "end": v(33, -90) * mm});
            skLineSegment(sketch, "E92.MirrorCS", {"start": v(15, -120) * mm, "end": v(15, -108) * mm});
            skLineSegment(sketch, "E93.MirrorCS", {"start": v(0, -120) * mm, "end": v(0, -90) * mm, "construction": true});
            skCircle(sketch, "E94.MirrorC", {"center": v(0, -120) * mm, "radius": 6 * mm});
            skSolve(sketch);
        }
        {
            var Q0;
            Q0 = qSketchRegion(id + "F16", true);
            var Q1;
            Q1=makeQuery(id+"F2.opExtrude","CAP_FACE",FACE,{"disambiguationData":[OSD([sQuery(id+"F0.wireOp",EDGE,"E12"),sQuery(id+"F0.wireOp",EDGE,"E13"),sQuery(id+"F0.wireOp",EDGE,"E14"),sQuery(id+"F0.wireOp",EDGE,"E15"),sQuery(id+"F0.wireOp",EDGE,"E17.filletArc"),sQuery(id+"F0.wireOp",EDGE,"E18.filletArc"),sQuery(id+"F0.wireOp",EDGE,"E19.filletArc"),sQuery(id+"F0.wireOp",EDGE,"E20.filletArc"),sQuery(id+"F0.wireOp",EDGE,"E25.0"),sQuery(id+"F0.wireOp",EDGE,"E25.1"),sQuery(id+"F0.wireOp",EDGE,"E25.2"),sQuery(id+"F0.wireOp",EDGE,"E25.3"),sQuery(id+"F0.wireOp",EDGE,"E25.4"),sQuery(id+"F0.wireOp",EDGE,"E25.5"),sQuery(id+"F0.wireOp",EDGE,"E25.6"),sQuery(id+"F0.wireOp",EDGE,"E25.7")])],"isStart":false});
            extrude(context, id + "F17", {"entities" : qUnion([Q0]), "endBound" : BoundingType.UP_TO_SURFACE, "depth" : 25 * mm, "endBoundEntityFace" : qUnion([Q1]), "offsetDistance" : 25 * mm});
        }
    });
